# Revit family: 3FR_63_UN_SM_Track 3Phase_ETK
name_source: partatom
category: Lighting Fixtures
units: mm (PartAtom-declared; Revit-internal decimal feet)

## family parameters
Always vertical = No
Cut with Voids When Loaded = No
Light Source = No
Part Type = Normal
Room Calculation Point = No
Round Connector Dimension = Use Diameter
Shared = No
Work Plane-Based = No

## types (2) — shared parameters
Apparent Load = 0 VA
Assembly Code = 63.00
Description = Track 3 Phases
IfcExportAs = IfcLightFixtureType
IfcExportType = POINTSOURCE
Manufacturer = ETK
Model = 3FR
URL = https://platform.ivlibrary.com
⌂ Powered by IVLibrary = www.ivlibrary.com

## per-type parameters (varying)
| type | Length |
| 3FR.1100.xx | 1000 mm  [stored 3.28084 ft] |
| 3FR.1300.xx | 3000 mm  [stored 9.84252 ft] |

note: [stored X ft] marks values corroborated as IEEE doubles in the binary element streams (Revit-internal decimal feet)

## geometry (parser evidence)
native form markers: Sweep x2
no freeform markers — native parametric forms only
